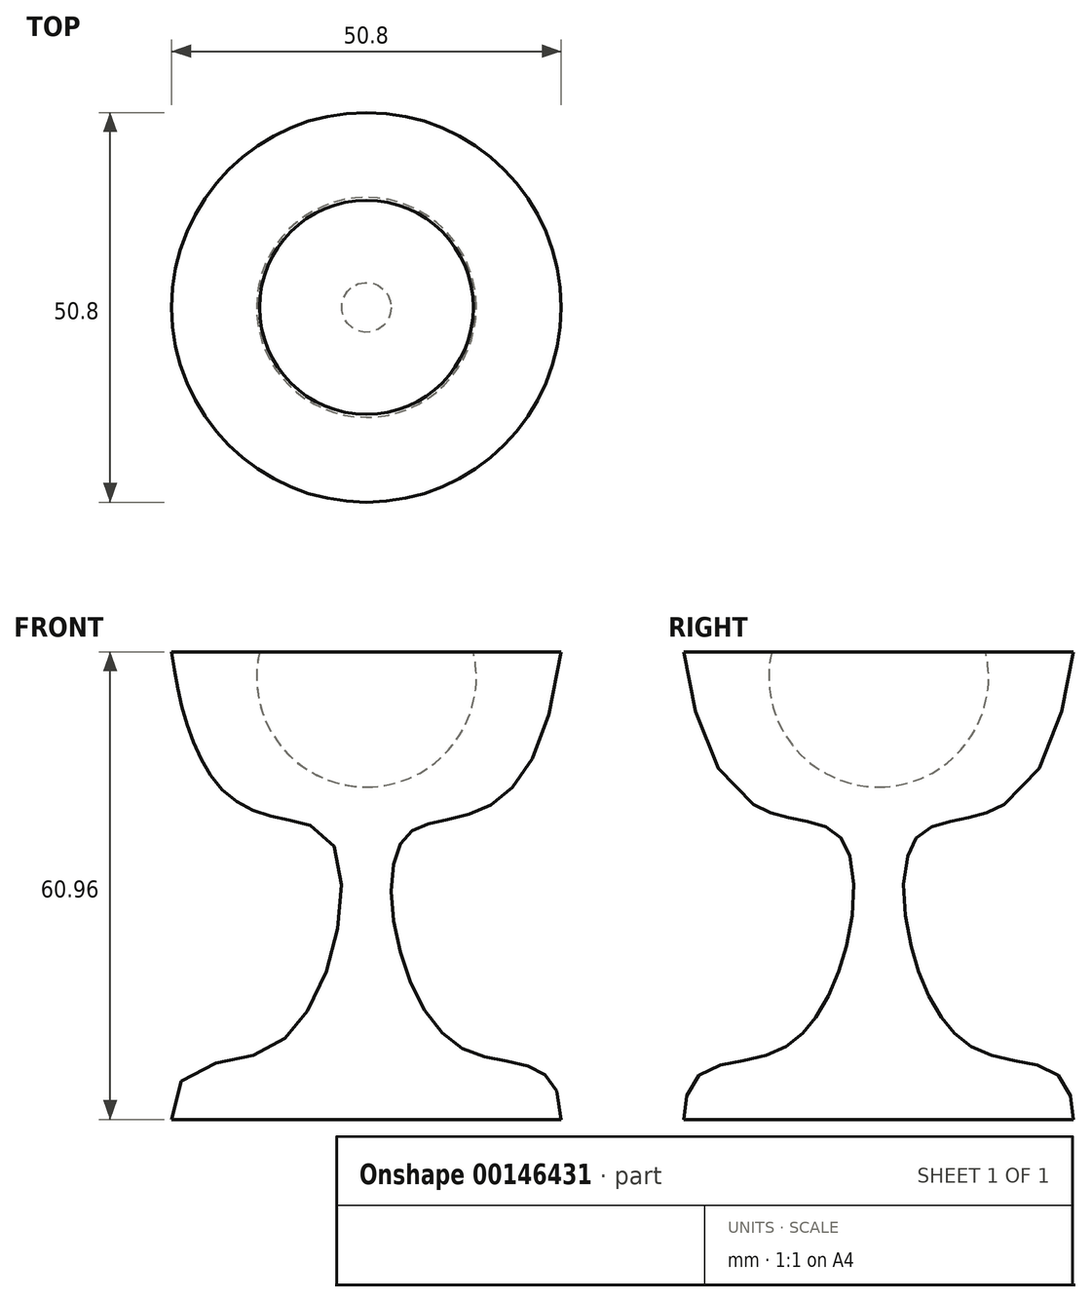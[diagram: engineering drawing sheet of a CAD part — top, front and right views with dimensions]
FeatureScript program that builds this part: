
annotation { "Feature Type Name" : "Feature", "Feature Type Description" : "" }
export const myFeature = defineFeature(function(context is Context, id is Id, definition is map)
    precondition{}
    {
        {
            var Q0;
            Q0=qCreatedBy(makeId("Top.planeOp"),FACE);
            var sketch = newSketch(context, id + "F0", { "sketchPlane" : qUnion([Q0])});
            skCircle(sketch, "E0", {"center": v(0, 0) * mm, "radius": 25.4 * mm});
            skSolve(sketch);
        }
        {
            var Q0;
            Q0 = qSketchRegion(id + "F0", true);
            extrude(context, id + "F1", {"entities" : qUnion([Q0]), "depth" : 60.96 * mm});
        }
        {
            var Q0;
            Q0=qCreatedBy(makeId("Front.planeOp"),FACE);
            var sketch = newSketch(context, id + "F2", { "sketchPlane" : qUnion([Q0])});
            skLineSegment(sketch, "E1", {"start": v(-25.4, 60.96) * mm, "end": v(-25.4, 0) * mm, "construction": true});
            skLineSegment(sketch, "E2", {"start": v(0, 70.54) * mm, "end": v(0, 5.46) * mm, "construction": true});
            skLineSegment(sketch, "E3", {"start": v(0, 5.46) * mm, "end": v(0, 0) * mm, "construction": true});
            skLineSegment(sketch, "E4", {"start": v(-62.16, 60.96) * mm, "end": v(74.79, 60.96) * mm, "construction": true});
            skFitSpline(sketch, "E5", {"points": [v(-25.4, 60.96) * mm, v(-4.88, 36.65) * mm, v(-11.75, 9.68) * mm, v(-25.4, 0) * mm], "startDerivative": vector(29.5, -219.4) * mm, "endDerivative": vector(0, -106.5) * mm});
            skLineSegment(sketch, "E6", {"start": v(-25.4, 60.96) * mm, "end": v(-25.4, 0) * mm});
            skSolve(sketch);
        }
        {
            var Q0;
            Q0 = qSketchRegion(id + "F2", true);
            var Q1;
            Q1=sQuery(id+"F2.wireOp",EDGE,"E2");
            revolve(context, id + "F3", {"operationType" : NewBodyOperationType.REMOVE, "entities" : qUnion([Q0]), "axis" : qUnion([Q1]), "revolveType" : RevolveType.FULL});
        }
        {
            var Q0;
            Q0=qCreatedBy(makeId("Front.planeOp"),FACE);
            var sketch = newSketch(context, id + "F4", { "sketchPlane" : qUnion([Q0])});
            skArc(sketch, "E7", {"start": v(0, 43.34) * mm, "mid": v(14.33, 57.67) * mm, "end": v(0, 72) * mm});
            skLineSegment(sketch, "E8", {"start": v(0, 72) * mm, "end": v(0, 43.34) * mm});
            skSolve(sketch);
        }
        {
            var Q0;
            Q0 = qSketchRegion(id + "F4", true);
            var Q1;
            Q1=sQuery(id+"F4.wireOp",EDGE,"E8");
            revolve(context, id + "F5", {"operationType" : NewBodyOperationType.REMOVE, "entities" : qUnion([Q0]), "axis" : qUnion([Q1]), "revolveType" : RevolveType.FULL, "oppositeDirection" : true});
        }
    });
